# Revit family: Urinal-waterless-Zurn-Z5795
name_source: partatom
category: Plumbing Fixtures
units: mm (PartAtom-declared; Revit-internal decimal feet)

## family parameters
Cut with Voids When Loaded = No
Host = Face
Maintain Annotation Orientation = No
OmniClass Number = 23.45.30.00
OmniClass Title = Washing and Waste Disposal Equipment
Part Type = Normal
Room Calculation Point = No
Round Connector Dimension = Use Radius
Shared = No

## types (1)
- Z5795 (WATERLESS URINAL)
    ADA Compliance = Yes
    Assembly Code = D2010.60
    Basin Depth = 8 "
    Basin Width = 14 "
    CW Connection = No
    CWFU = 0
    Default Elevation = 48 "
    Depth = 14.25 "
    Description = Waterless Urinal
    Distance from Floor to Rim = 17 "
    Distence from Rim to Center of Sanitary (F/B) = 3.75 "
    HW Connection = No
    HWFU = 0
    Height = 26.75 "
    Main Material = Finishes - Zurn - Vitreous_White
    Manufacturer = Zurn Water, LLC
    Manufacturer Brand = Zurn
    Model = Z5795
    Modified Date = 11/25/2025
    Oulet Connection Size (inch) = 1 "
    Product Documentation Link = https://files.zurn.com
    Product Installation Sheet URL = https://files.zurn.com
    Product Page URL = https://www.zurn.com
    Product data URL = https://www.bimobject.com
    Shipping Weight (lbs) = 66
    URL = https://www.zurn.com
    Vent Connection = No
    WFU = 1
    Waste Connection = Yes
    Width = 19 "

## geometry (parser evidence)
native form markers: Sweep x4
no freeform markers — native parametric forms only
